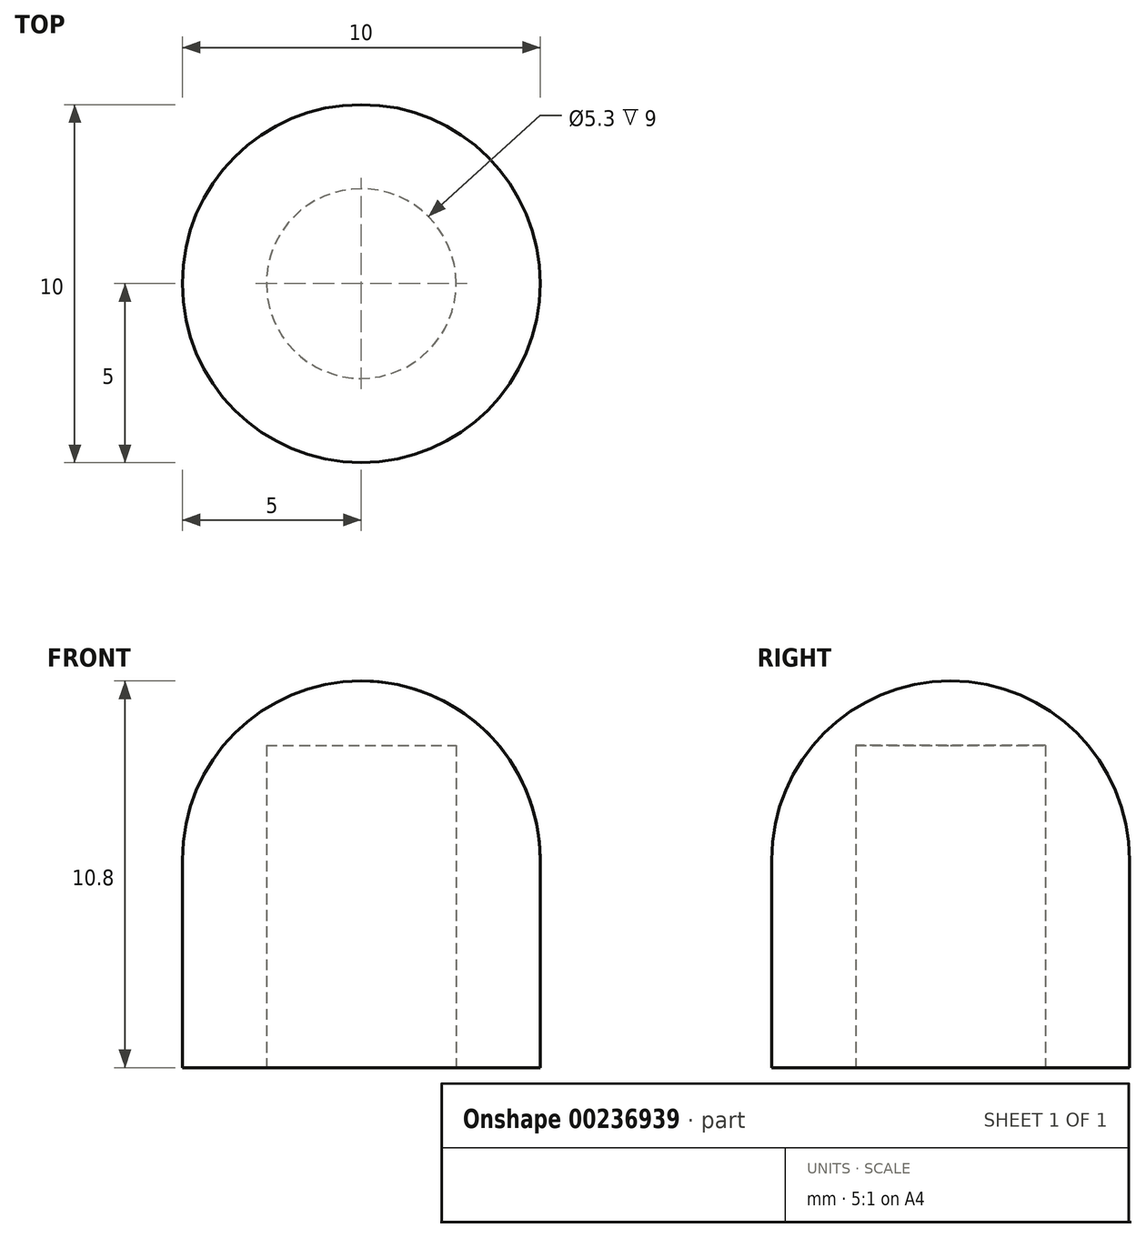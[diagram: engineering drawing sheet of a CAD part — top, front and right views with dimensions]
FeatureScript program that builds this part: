
annotation { "Feature Type Name" : "Feature", "Feature Type Description" : "" }
export const myFeature = defineFeature(function(context is Context, id is Id, definition is map)
    precondition{}
    {
        {
            var Q0;
            Q0=qCreatedBy(makeId("Top.planeOp"),FACE);
            var sketch = newSketch(context, id + "F0", { "sketchPlane" : qUnion([Q0])});
            skCircle(sketch, "E0", {"center": v(0, 0) * mm, "radius": 5 * mm});
            skSolve(sketch);
        }
        {
            var Q0;
            Q0 = qSketchRegion(id + "F0", true);
            extrude(context, id + "F1", {"entities" : qUnion([Q0]), "depth" : 10.8 * mm});
        }
        {
            var Q0;
            Q0=makeQuery(id+"F1.opExtrude","CAP_EDGE",EDGE,{"disambiguationData":[OSD([sQuery(id+"F0.wireOp",EDGE,"E0")])],"isStart":false});
            fillet(context, id + "F2", {"entities" : qUnion([Q0]), "radius" : 5 * mm, "tangentPropagation" : true, "allowEdgeOverflow" : false});
        }
        {
            var Q0;
            Q0=makeQuery(id+"F1.opExtrude","CAP_FACE",FACE,{"disambiguationData":[OSD([sQuery(id+"F0.wireOp",EDGE,"E0")])],"isStart":true});
            var sketch = newSketch(context, id + "F3", { "sketchPlane" : qUnion([Q0])});
            skCircle(sketch, "E1", {"center": v(0, 0) * mm, "radius": 2.65 * mm});
            skSolve(sketch);
        }
        {
            var Q0;
            Q0=makeQuery(id+"F3.imprint","IMPRINT",FACE,{"disambiguationData":[TD([[makeQuery(id+"F3.imprint","IMPRINT",EDGE,{"derivedFrom":sQuery(id+"F3.wireOp",EDGE,"E1")}),1.0]])]});
            extrude(context, id + "F4", {"entities" : qUnion([Q0]), "operationType" : NewBodyOperationType.REMOVE, "oppositeDirection" : true, "depth" : 9 * mm});
        }
    });
